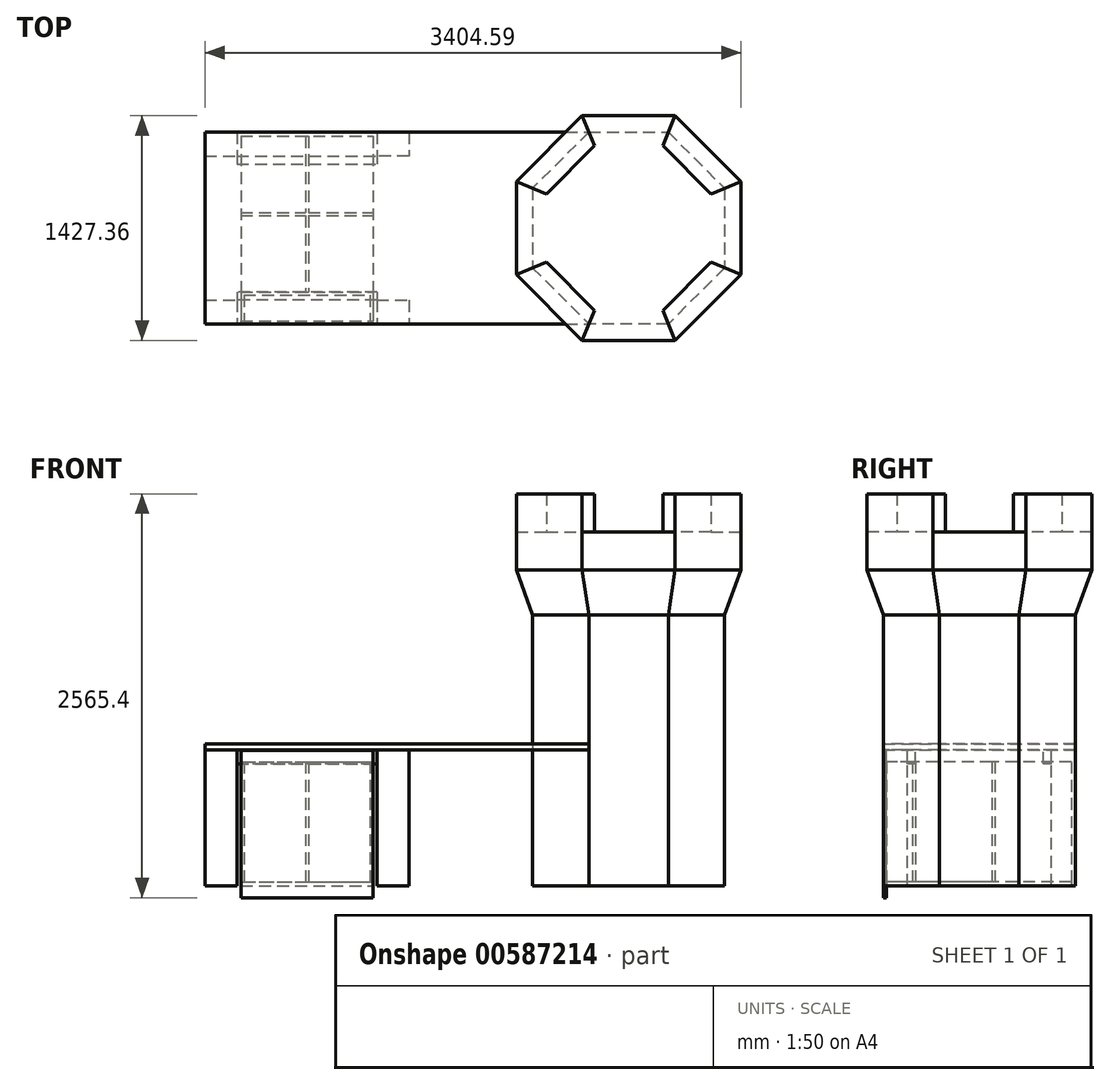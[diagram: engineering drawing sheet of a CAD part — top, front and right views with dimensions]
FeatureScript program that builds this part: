
annotation { "Feature Type Name" : "Feature", "Feature Type Description" : "" }
export const myFeature = defineFeature(function(context is Context, id is Id, definition is map)
    precondition{}
    {
        {
            var Q0;
            Q0=qCreatedBy(makeId("Front.planeOp"),FACE);
            var sketch = newSketch(context, id + "F0", { "sketchPlane" : qUnion([Q0])});
            skLineSegment(sketch, "E0.bottom", {"start": v(1219.2, 0) * mm, "end": v(-1219.2, 0) * mm, "construction": true});
            skLineSegment(sketch, "E0.top", {"start": v(1219.2, -863.6) * mm, "end": v(-1219.2, -863.6) * mm, "construction": true});
            skLineSegment(sketch, "E0.left", {"start": v(1219.2, 0) * mm, "end": v(1219.2, -863.6) * mm, "construction": true});
            skLineSegment(sketch, "E0.right", {"start": v(-1219.2, 0) * mm, "end": v(-1219.2, -863.6) * mm, "construction": true});
            skLineSegment(sketch, "E1", {"start": v(152.4, 0) * mm, "end": v(152.4, -863.6) * mm, "construction": true});
            skLineSegment(sketch, "E2", {"start": v(190.5, 0) * mm, "end": v(190.5, -863.6) * mm, "construction": true});
            skLineSegment(sketch, "E3", {"start": v(-1016, 0) * mm, "end": v(-1016, -863.6) * mm, "construction": true});
            skLineSegment(sketch, "E4", {"start": v(-3657.6, 1778) * mm, "end": v(8534.4, 1778) * mm, "construction": true});
            skLineSegment(sketch, "E5", {"start": v(8534.4, 1778) * mm, "end": v(8534.4, -965.2) * mm, "construction": true});
            skLineSegment(sketch, "E6", {"start": v(8534.4, -965.2) * mm, "end": v(-3657.6, -965.2) * mm, "construction": true});
            skLineSegment(sketch, "E7", {"start": v(-3657.6, -965.2) * mm, "end": v(-3657.6, 1778) * mm, "construction": true});
            skLineSegment(sketch, "E8", {"start": v(-1219.2, 1219.2) * mm, "end": v(1219.2, 1219.2) * mm, "construction": true});
            skLineSegment(sketch, "E9", {"start": v(1054.1, 1143) * mm, "end": v(1054.1, 1625.6) * mm, "construction": true});
            skLineSegment(sketch, "E10", {"start": v(1054.1, 1625.6) * mm, "end": v(2079.7, 1625.6) * mm, "construction": true});
            skLineSegment(sketch, "E11", {"start": v(1054.1, 1143) * mm, "end": v(1219.2, 857.04) * mm, "construction": true});
            skLineSegment(sketch, "E12", {"start": v(1219.2, 857.04) * mm, "end": v(1219.2, 0) * mm, "construction": true});
            skLineSegment(sketch, "E13", {"start": v(1054.1, 1384.3) * mm, "end": v(2079.7, 1384.3) * mm, "construction": true});
            skSolve(sketch);
        }
        {
            var Q0;
            Q0=qCreatedBy(makeId("Top.planeOp"),FACE);
            var sketch = newSketch(context, id + "F1", { "sketchPlane" : qUnion([Q0])});
            skLineSegment(sketch, "E14.bottom", {"start": v(-1219.2, -609.6) * mm, "end": v(1219.2, -609.6) * mm, "construction": true});
            skLineSegment(sketch, "E14.top", {"start": v(-1219.2, 609.6) * mm, "end": v(1219.2, 609.6) * mm, "construction": true});
            skLineSegment(sketch, "E14.left", {"start": v(-1219.2, -609.6) * mm, "end": v(-1219.2, 609.6) * mm, "construction": true});
            skLineSegment(sketch, "E14.right", {"start": v(1219.2, -609.6) * mm, "end": v(1219.2, 609.6) * mm, "construction": true});
            skPoint(sketch, "E14.middle", {"position": v(0, 0) * mm});
            skLineSegment(sketch, "E15", {"start": v(1219.2, 609.6) * mm, "end": v(862.1, 252.5) * mm, "construction": true});
            skLineSegment(sketch, "E16", {"start": v(862.1, 252.5) * mm, "end": v(862.1, -252.5) * mm, "construction": true});
            skLineSegment(sketch, "E17", {"start": v(862.1, -252.5) * mm, "end": v(1219.2, -609.6) * mm, "construction": true});
            skLineSegment(sketch, "E18.bottom", {"start": v(-1219.2, 609.6) * mm, "end": v(-1016, 609.6) * mm, "construction": true});
            skLineSegment(sketch, "E18.top", {"start": v(-1219.2, 457.2) * mm, "end": v(-1016, 457.2) * mm, "construction": true});
            skLineSegment(sketch, "E18.left", {"start": v(-1219.2, 609.6) * mm, "end": v(-1219.2, 457.2) * mm, "construction": true});
            skLineSegment(sketch, "E18.right", {"start": v(-1016, 609.6) * mm, "end": v(-1016, 457.2) * mm, "construction": true});
            skLineSegment(sketch, "E19.bottom", {"start": v(-1219.2, -609.6) * mm, "end": v(-1016, -609.6) * mm, "construction": true});
            skLineSegment(sketch, "E19.top", {"start": v(-1219.2, -457.2) * mm, "end": v(-1016, -457.2) * mm, "construction": true});
            skLineSegment(sketch, "E19.left", {"start": v(-1219.2, -609.6) * mm, "end": v(-1219.2, -457.2) * mm, "construction": true});
            skLineSegment(sketch, "E19.right", {"start": v(-1016, -609.6) * mm, "end": v(-1016, -457.2) * mm, "construction": true});
            skLineSegment(sketch, "E20.bottom", {"start": v(1219.2, 609.6) * mm, "end": v(1016, 609.6) * mm, "construction": true});
            skLineSegment(sketch, "E20.top", {"start": v(1219.2, 457.2) * mm, "end": v(1016, 457.2) * mm, "construction": true});
            skLineSegment(sketch, "E20.left", {"start": v(1219.2, 609.6) * mm, "end": v(1219.2, 457.2) * mm, "construction": true});
            skLineSegment(sketch, "E20.right", {"start": v(1016, 609.6) * mm, "end": v(1016, 457.2) * mm});
            skLineSegment(sketch, "E21.bottom", {"start": v(1219.2, -609.6) * mm, "end": v(1016, -609.6) * mm, "construction": true});
            skLineSegment(sketch, "E21.top", {"start": v(1219.2, -457.2) * mm, "end": v(1016, -457.2) * mm, "construction": true});
            skLineSegment(sketch, "E21.left", {"start": v(1219.2, -609.6) * mm, "end": v(1219.2, -457.2) * mm, "construction": true});
            skLineSegment(sketch, "E21.right", {"start": v(1016, -609.6) * mm, "end": v(1016, -457.2) * mm});
            skLineSegment(sketch, "E22", {"start": v(-1016, 609.6) * mm, "end": v(-1016, -609.6) * mm, "construction": true});
            skLineSegment(sketch, "E23.bottom", {"start": v(-977.9, 406.4) * mm, "end": v(-571.5, 406.4) * mm, "construction": true});
            skLineSegment(sketch, "E23.top", {"start": v(-977.9, 0) * mm, "end": v(-571.5, 0) * mm, "construction": true});
            skLineSegment(sketch, "E23.left", {"start": v(-977.9, 406.4) * mm, "end": v(-977.9, 0) * mm, "construction": true});
            skLineSegment(sketch, "E23.right", {"start": v(-571.5, 406.4) * mm, "end": v(-571.5, 0) * mm, "construction": true});
            skLineSegment(sketch, "E24.top", {"start": v(-571.5, -406.4) * mm, "end": v(-977.9, -406.4) * mm, "construction": true});
            skLineSegment(sketch, "E24.left", {"start": v(-571.5, 0) * mm, "end": v(-571.5, -406.4) * mm, "construction": true});
            skLineSegment(sketch, "E25.top", {"start": v(-571.5, 406.4) * mm, "end": v(-165.1, 406.4) * mm, "construction": true});
            skLineSegment(sketch, "E25.right", {"start": v(-165.1, 0) * mm, "end": v(-165.1, 406.4) * mm, "construction": true});
            skLineSegment(sketch, "E26.bottom", {"start": v(-165.1, 0) * mm, "end": v(-571.5, 0) * mm, "construction": true});
            skLineSegment(sketch, "E26.top", {"start": v(-165.1, -406.4) * mm, "end": v(-571.5, -406.4) * mm, "construction": true});
            skLineSegment(sketch, "E26.left", {"start": v(-165.1, 0) * mm, "end": v(-165.1, -406.4) * mm, "construction": true});
            skLineSegment(sketch, "E27", {"start": v(-571.5, 406.4) * mm, "end": v(-571.5, 609.6) * mm, "construction": true});
            skLineSegment(sketch, "E28", {"start": v(-571.5, -406.4) * mm, "end": v(-571.5, -609.6) * mm, "construction": true});
            skLineSegment(sketch, "E29", {"start": v(-977.9, 0) * mm, "end": v(-977.9, -406.4) * mm, "construction": true});
            skLineSegment(sketch, "E30", {"start": v(1219.2, 609.6) * mm, "end": v(1724.2, 609.6) * mm, "construction": true});
            skLineSegment(sketch, "E31", {"start": v(1724.2, 609.6) * mm, "end": v(2081.3, 252.5) * mm, "construction": true});
            skLineSegment(sketch, "E32", {"start": v(2081.3, 252.5) * mm, "end": v(2081.3, -252.5) * mm, "construction": true});
            skLineSegment(sketch, "E33", {"start": v(2081.3, -252.5) * mm, "end": v(1724.2, -609.6) * mm, "construction": true});
            skLineSegment(sketch, "E34", {"start": v(1724.2, -609.6) * mm, "end": v(1219.2, -609.6) * mm, "construction": true});
            skLineSegment(sketch, "E35", {"start": v(-127, 609.6) * mm, "end": v(-127, -609.6) * mm, "construction": true});
            skLineSegment(sketch, "E36.bottom", {"start": v(-127, 609.6) * mm, "end": v(76.2, 609.6) * mm, "construction": true});
            skLineSegment(sketch, "E36.top", {"start": v(-127, 457.2) * mm, "end": v(76.2, 457.2) * mm, "construction": true});
            skLineSegment(sketch, "E36.left", {"start": v(-127, 609.6) * mm, "end": v(-127, 457.2) * mm, "construction": true});
            skLineSegment(sketch, "E36.right", {"start": v(76.2, 609.6) * mm, "end": v(76.2, 457.2) * mm, "construction": true});
            skLineSegment(sketch, "E37.bottom", {"start": v(-127, -609.6) * mm, "end": v(76.2, -609.6) * mm, "construction": true});
            skLineSegment(sketch, "E37.top", {"start": v(-127, -457.2) * mm, "end": v(76.2, -457.2) * mm, "construction": true});
            skLineSegment(sketch, "E37.left", {"start": v(-127, -609.6) * mm, "end": v(-127, -457.2) * mm, "construction": true});
            skLineSegment(sketch, "E37.right", {"start": v(76.2, -609.6) * mm, "end": v(76.2, -457.2) * mm, "construction": true});
            skSolve(sketch);
        }
        {
            var Q0;
            Q0=qCreatedBy(makeId("Top.planeOp"),FACE);
            var sketch = newSketch(context, id + "F2", { "sketchPlane" : qUnion([Q0])});
            skLineSegment(sketch, "E38.bottom", {"start": v(-1219.2, -609.6) * mm, "end": v(1219.2, -609.6) * mm});
            skLineSegment(sketch, "E38.top", {"start": v(-1219.2, 609.6) * mm, "end": v(1219.2, 609.6) * mm});
            skLineSegment(sketch, "E38.left", {"start": v(-1219.2, -609.6) * mm, "end": v(-1219.2, 609.6) * mm});
            skLineSegment(sketch, "E38.right", {"start": v(1219.2, -609.6) * mm, "end": v(1219.2, 609.6) * mm, "construction": true});
            skLineSegment(sketch, "E39.0", {"start": v(1219.2, 609.6) * mm, "end": v(862.1, 252.5) * mm});
            skLineSegment(sketch, "E40.0", {"start": v(862.1, 252.5) * mm, "end": v(862.1, -252.5) * mm});
            skLineSegment(sketch, "E40.1", {"start": v(862.1, -252.5) * mm, "end": v(1219.2, -609.6) * mm});
            skSolve(sketch);
        }
        {
            var Q0;
            Q0 = qSketchRegion(id + "F2", true);
            extrude(context, id + "F3", {"entities" : qUnion([Q0]), "depth" : 38.1 * mm, "offsetDistance" : 25.4 * mm});
        }
        {
            var Q0;
            Q0=qCreatedBy(makeId("Top.planeOp"),FACE);
            var sketch = newSketch(context, id + "F4", { "sketchPlane" : qUnion([Q0])});
            skLineSegment(sketch, "E41.bottom", {"start": v(-1219.2, 609.6) * mm, "end": v(-1016, 609.6) * mm});
            skLineSegment(sketch, "E41.top", {"start": v(-1219.2, 457.2) * mm, "end": v(-1016, 457.2) * mm});
            skLineSegment(sketch, "E41.left", {"start": v(-1219.2, 609.6) * mm, "end": v(-1219.2, 457.2) * mm});
            skLineSegment(sketch, "E41.right", {"start": v(-1016, 609.6) * mm, "end": v(-1016, 457.2) * mm});
            skLineSegment(sketch, "E42.bottom", {"start": v(-1219.2, -457.2) * mm, "end": v(-1016, -457.2) * mm});
            skLineSegment(sketch, "E42.top", {"start": v(-1219.2, -609.6) * mm, "end": v(-1016, -609.6) * mm});
            skLineSegment(sketch, "E42.left", {"start": v(-1219.2, -457.2) * mm, "end": v(-1219.2, -609.6) * mm});
            skLineSegment(sketch, "E42.right", {"start": v(-1016, -457.2) * mm, "end": v(-1016, -609.6) * mm});
            skLineSegment(sketch, "E43.bottom", {"start": v(76.2, 609.6) * mm, "end": v(-127, 609.6) * mm});
            skLineSegment(sketch, "E43.top", {"start": v(76.2, 457.2) * mm, "end": v(-127, 457.2) * mm});
            skLineSegment(sketch, "E43.left", {"start": v(76.2, 609.6) * mm, "end": v(76.2, 457.2) * mm});
            skLineSegment(sketch, "E43.right", {"start": v(-127, 609.6) * mm, "end": v(-127, 457.2) * mm});
            skLineSegment(sketch, "E44.bottom", {"start": v(-127, -457.2) * mm, "end": v(76.2, -457.2) * mm});
            skLineSegment(sketch, "E44.top", {"start": v(-127, -609.6) * mm, "end": v(76.2, -609.6) * mm});
            skLineSegment(sketch, "E44.left", {"start": v(-127, -457.2) * mm, "end": v(-127, -609.6) * mm});
            skLineSegment(sketch, "E44.right", {"start": v(76.2, -457.2) * mm, "end": v(76.2, -609.6) * mm});
            skSolve(sketch);
        }
        {
            var Q0;
            Q0 = qSketchRegion(id + "F4", true);
            var Q1;
            Q1=sQuery(id+"F0.wireOp",VERTEX,"E0.right.end");
            extrude(context, id + "F5", {"entities" : qUnion([Q0]), "endBound" : BoundingType.UP_TO_VERTEX, "oppositeDirection" : true, "depth" : 25.4 * mm, "endBoundEntityVertex" : qUnion([Q1]), "offsetDistance" : 25.4 * mm});
        }
        {
            var Q0;
            Q0=qCreatedBy(makeId("Front.planeOp"),FACE);
            var Q1;
            Q1=sQuery(id+"F1.wireOp",VERTEX,"E14.left.start");
            cPlane(context, id + "F6", {"entities" : qUnion([Q0, Q1]), "cplaneType" : CPlaneType.PLANE_POINT, "offset" : 25.4 * mm, "width" : 152.4 * mm, "height" : 152.4 * mm});
        }
        {
            var Q0;
            Q0=qCreatedBy(makeId("Top.planeOp"),FACE);
            var sketch = newSketch(context, id + "F7", { "sketchPlane" : qUnion([Q0])});
            skLineSegment(sketch, "E45.0", {"start": v(1724.2, -609.6) * mm, "end": v(1219.2, -609.6) * mm});
            skLineSegment(sketch, "E45.1", {"start": v(2081.3, -252.5) * mm, "end": v(1724.2, -609.6) * mm});
            skLineSegment(sketch, "E45.2", {"start": v(2081.3, 252.5) * mm, "end": v(2081.3, -252.5) * mm});
            skLineSegment(sketch, "E45.3", {"start": v(1724.2, 609.6) * mm, "end": v(2081.3, 252.5) * mm});
            skLineSegment(sketch, "E45.4", {"start": v(1219.2, 609.6) * mm, "end": v(1724.2, 609.6) * mm});
            skLineSegment(sketch, "E45.5", {"start": v(1219.2, 609.6) * mm, "end": v(862.1, 252.5) * mm});
            skLineSegment(sketch, "E45.6", {"start": v(862.1, 252.5) * mm, "end": v(862.1, -252.5) * mm});
            skLineSegment(sketch, "E45.7", {"start": v(862.1, -252.5) * mm, "end": v(1219.2, -609.6) * mm});
            skSolve(sketch);
        }
        {
            var Q0;
            Q0=makeQuery(id+"F7.imprint","IMPRINT",FACE,{"disambiguationData":[TD([[makeQuery(id+"F7.imprint","IMPRINT",EDGE,{"derivedFrom":sQuery(id+"F7.wireOp",EDGE,"E45.0")}),-1.0]])]});
            var Q1;
            Q1 = qConstructionFilter(qBodyType(qCreatedBy(id + "F7" ,EDGE), BodyType.WIRE), ConstructionObject.NO);
            var Q2;
            Q2=sQuery(id+"F0.wireOp",VERTEX,"E0.left.end");
            var Q3;
            Q3=sQuery(id+"F0.wireOp",VERTEX,"E12.start");
            extrude(context, id + "F8", {"entities" : qUnion([Q0]), "surfaceEntities" : qUnion([Q1]), "endBound" : BoundingType.UP_TO_VERTEX, "oppositeDirection" : true, "depth" : 25.4 * mm, "endBoundEntityVertex" : qUnion([Q2]), "offsetDistance" : 25.4 * mm, "hasSecondDirection" : true, "secondDirectionBound" : SecondDirectionBoundingType.UP_TO_VERTEX, "secondDirectionOppositeDirection" : false, "secondDirectionDepth" : 25.4 * mm, "secondDirectionBoundEntityVertex" : qUnion([Q3])});
        }
        {
            var Q0;
            Q0=makeQuery(id+"F8.opExtrude","CAP_FACE",FACE,{"disambiguationData":[OSD([sQuery(id+"F7.wireOp",EDGE,"E45.0"),sQuery(id+"F7.wireOp",EDGE,"E45.1"),sQuery(id+"F7.wireOp",EDGE,"E45.2"),sQuery(id+"F7.wireOp",EDGE,"E45.3"),sQuery(id+"F7.wireOp",EDGE,"E45.4"),sQuery(id+"F7.wireOp",EDGE,"E45.5"),sQuery(id+"F7.wireOp",EDGE,"E45.6"),sQuery(id+"F7.wireOp",EDGE,"E45.7")])],"isStart":true});
            var sketch = newSketch(context, id + "F9", { "sketchPlane" : qUnion([Q0])});
            skSolve(sketch);
        }
        {
            var Q0;
            Q0 = qSketchRegion(id + "F9", true);
            var Q1;
            Q1=makeQuery(id+"F9.imprint","IMPRINT",FACE,{"disambiguationData":[TD([[makeQuery(id+"F9.imprint","IMPRINT",EDGE,{"derivedFrom":makeQuery(id+"F8.opExtrude","CAP_EDGE",EDGE,{"disambiguationData":[OSD([sQuery(id+"F7.wireOp",EDGE,"E45.0")])],"isStart":true})}),-1.0]])]});
            var Q2;
            Q2=sQuery(id+"F0.wireOp",VERTEX,"E9.start");
            extrude(context, id + "F10", {"entities" : qUnion([Q0, Q1]), "operationType" : NewBodyOperationType.ADD, "endBound" : BoundingType.UP_TO_VERTEX, "depth" : 25.4 * mm, "endBoundEntityVertex" : qUnion([Q2]), "offsetDistance" : 25.4 * mm, "hasDraft" : true, "draftAngle" : 20 * degree});
        }
        {
            var Q0;
            Q0=makeQuery(id+"F10.opExtrude","CAP_FACE",FACE,{"disambiguationData":[OSD([sQuery(id+"F7.wireOp",EDGE,"E45.0"),sQuery(id+"F7.wireOp",EDGE,"E45.1"),sQuery(id+"F7.wireOp",EDGE,"E45.2"),sQuery(id+"F7.wireOp",EDGE,"E45.3"),sQuery(id+"F7.wireOp",EDGE,"E45.4"),sQuery(id+"F7.wireOp",EDGE,"E45.5"),sQuery(id+"F7.wireOp",EDGE,"E45.6"),sQuery(id+"F7.wireOp",EDGE,"E45.7")])],"isStart":false});
            var sketch = newSketch(context, id + "F11", { "sketchPlane" : qUnion([Q0])});
            skLineSegment(sketch, "E46.0", {"start": v(1176.09, 713.68) * mm, "end": v(758.02, 295.62) * mm});
            skLineSegment(sketch, "E46.1", {"start": v(1176.09, 713.68) * mm, "end": v(1767.32, 713.68) * mm});
            skLineSegment(sketch, "E46.2", {"start": v(1767.32, 713.68) * mm, "end": v(2185.39, 295.62) * mm});
            skLineSegment(sketch, "E46.3", {"start": v(2185.39, 295.62) * mm, "end": v(2185.39, -295.62) * mm});
            skLineSegment(sketch, "E46.4", {"start": v(2185.39, -295.62) * mm, "end": v(1767.32, -713.68) * mm});
            skLineSegment(sketch, "E46.5", {"start": v(1767.32, -713.68) * mm, "end": v(1176.09, -713.68) * mm});
            skLineSegment(sketch, "E46.6", {"start": v(758.02, -295.62) * mm, "end": v(1176.09, -713.68) * mm});
            skLineSegment(sketch, "E46.7", {"start": v(758.02, 295.62) * mm, "end": v(758.02, -295.62) * mm});
            skSolve(sketch);
        }
        {
            var Q0;
            Q0 = qSketchRegion(id + "F11", true);
            var Q1;
            Q1=sQuery(id+"F0.wireOp",VERTEX,"E13.start");
            extrude(context, id + "F12", {"entities" : qUnion([Q0]), "operationType" : NewBodyOperationType.ADD, "endBound" : BoundingType.UP_TO_VERTEX, "depth" : 25.4 * mm, "endBoundEntityVertex" : qUnion([Q1]), "offsetDistance" : 25.4 * mm});
        }
        {
            var Q0;
            Q0=makeQuery(id+"F12.opExtrude","CAP_FACE",FACE,{"disambiguationData":[OSD([sQuery(id+"F11.wireOp",EDGE,"E46.0"),sQuery(id+"F11.wireOp",EDGE,"E46.1"),sQuery(id+"F11.wireOp",EDGE,"E46.2"),sQuery(id+"F11.wireOp",EDGE,"E46.3"),sQuery(id+"F11.wireOp",EDGE,"E46.4"),sQuery(id+"F11.wireOp",EDGE,"E46.5"),sQuery(id+"F11.wireOp",EDGE,"E46.6"),sQuery(id+"F11.wireOp",EDGE,"E46.7")])],"isStart":false});
            var sketch = newSketch(context, id + "F13", { "sketchPlane" : qUnion([Q0])});
            skLineSegment(sketch, "E47.0", {"start": v(1176.09, 713.68) * mm, "end": v(758.02, 295.62) * mm});
            skLineSegment(sketch, "E47.1", {"start": v(1176.09, 713.68) * mm, "end": v(1767.32, 713.68) * mm, "construction": true});
            skLineSegment(sketch, "E47.2", {"start": v(1767.32, 713.68) * mm, "end": v(2185.39, 295.62) * mm});
            skLineSegment(sketch, "E47.3", {"start": v(2185.39, 295.62) * mm, "end": v(2185.39, -295.62) * mm, "construction": true});
            skLineSegment(sketch, "E47.4", {"start": v(2185.39, -295.62) * mm, "end": v(1767.32, -713.68) * mm});
            skLineSegment(sketch, "E47.5", {"start": v(1767.32, -713.68) * mm, "end": v(1176.09, -713.68) * mm, "construction": true});
            skLineSegment(sketch, "E47.6", {"start": v(758.02, -295.62) * mm, "end": v(1176.09, -713.68) * mm});
            skLineSegment(sketch, "E47.7", {"start": v(758.02, 295.62) * mm, "end": v(758.02, -295.62) * mm, "construction": true});
            skLineSegment(sketch, "E48.0", {"start": v(1255, 523.18) * mm, "end": v(948.52, 216.7) * mm});
            skLineSegment(sketch, "E48.1", {"start": v(948.52, 216.7) * mm, "end": v(948.52, -216.7) * mm, "construction": true});
            skLineSegment(sketch, "E48.2", {"start": v(1255, 523.18) * mm, "end": v(1688.41, 523.18) * mm, "construction": true});
            skLineSegment(sketch, "E48.3", {"start": v(948.52, -216.7) * mm, "end": v(1255, -523.18) * mm});
            skLineSegment(sketch, "E48.4", {"start": v(1688.41, 523.18) * mm, "end": v(1994.89, 216.7) * mm});
            skLineSegment(sketch, "E48.5", {"start": v(1994.89, 216.7) * mm, "end": v(1994.89, -216.7) * mm, "construction": true});
            skLineSegment(sketch, "E48.6", {"start": v(1994.89, -216.7) * mm, "end": v(1688.41, -523.18) * mm});
            skLineSegment(sketch, "E48.7", {"start": v(1688.41, -523.18) * mm, "end": v(1255, -523.18) * mm, "construction": true});
            skLineSegment(sketch, "E49", {"start": v(1176.09, 713.68) * mm, "end": v(1255, 523.18) * mm});
            skLineSegment(sketch, "E50", {"start": v(1767.32, 713.68) * mm, "end": v(1688.41, 523.18) * mm});
            skLineSegment(sketch, "E51", {"start": v(1994.89, 216.7) * mm, "end": v(2185.39, 295.62) * mm});
            skLineSegment(sketch, "E52", {"start": v(1994.89, -216.7) * mm, "end": v(2185.39, -295.62) * mm});
            skLineSegment(sketch, "E53", {"start": v(1688.41, -523.18) * mm, "end": v(1767.32, -713.68) * mm});
            skLineSegment(sketch, "E54", {"start": v(1255, -523.18) * mm, "end": v(1176.09, -713.68) * mm});
            skLineSegment(sketch, "E55", {"start": v(948.52, -216.7) * mm, "end": v(758.02, -295.62) * mm});
            skLineSegment(sketch, "E56", {"start": v(758.02, 295.62) * mm, "end": v(948.52, 216.7) * mm});
            skSolve(sketch);
        }
        {
            var Q0;
            Q0 = qSketchRegion(id + "F13", true);
            var Q1;
            Q1=sQuery(id+"F0.wireOp",VERTEX,"E9.end");
            extrude(context, id + "F14", {"entities" : qUnion([Q0]), "operationType" : NewBodyOperationType.ADD, "endBound" : BoundingType.UP_TO_VERTEX, "depth" : 25.4 * mm, "endBoundEntityVertex" : qUnion([Q1]), "offsetDistance" : 25.4 * mm});
        }
        {
            var Q0;
            Q0=qCreatedBy(makeId("Top.planeOp"),FACE);
            var sketch = newSketch(context, id + "F15", { "sketchPlane" : qUnion([Q0])});
            skLineSegment(sketch, "E57.bottom", {"start": v(-1016, 457.2) * mm, "end": v(-127, 457.2) * mm});
            skLineSegment(sketch, "E57.top", {"start": v(-1016, 406.4) * mm, "end": v(-127, 406.4) * mm});
            skLineSegment(sketch, "E57.left", {"start": v(-1016, 457.2) * mm, "end": v(-1016, 406.4) * mm});
            skLineSegment(sketch, "E57.right", {"start": v(-127, 457.2) * mm, "end": v(-127, 406.4) * mm});
            skLineSegment(sketch, "E58.bottom", {"start": v(-127, 406.4) * mm, "end": v(-165.1, 406.4) * mm});
            skLineSegment(sketch, "E58.top", {"start": v(-127, -406.4) * mm, "end": v(-165.1, -406.4) * mm});
            skLineSegment(sketch, "E58.left", {"start": v(-127, 406.4) * mm, "end": v(-127, -406.4) * mm});
            skLineSegment(sketch, "E58.right", {"start": v(-165.1, 406.4) * mm, "end": v(-165.1, -406.4) * mm});
            skLineSegment(sketch, "E59.bottom", {"start": v(-127, -406.4) * mm, "end": v(-1016, -406.4) * mm});
            skLineSegment(sketch, "E59.top", {"start": v(-127, -457.2) * mm, "end": v(-1016, -457.2) * mm});
            skLineSegment(sketch, "E59.left", {"start": v(-127, -406.4) * mm, "end": v(-127, -457.2) * mm});
            skLineSegment(sketch, "E59.right", {"start": v(-1016, -406.4) * mm, "end": v(-1016, -457.2) * mm});
            skLineSegment(sketch, "E60.bottom", {"start": v(-1016, -406.4) * mm, "end": v(-977.9, -406.4) * mm});
            skLineSegment(sketch, "E60.top", {"start": v(-1016, 406.4) * mm, "end": v(-977.9, 406.4) * mm});
            skLineSegment(sketch, "E60.left", {"start": v(-1016, -406.4) * mm, "end": v(-1016, 406.4) * mm});
            skLineSegment(sketch, "E60.right", {"start": v(-977.9, -406.4) * mm, "end": v(-977.9, 406.4) * mm});
            skSolve(sketch);
        }
        {
            var Q0;
            Q0=makeQuery(id+"F15.imprint","IMPRINT",FACE,{"disambiguationData":[TD([[makeQuery(id+"F15.imprint","IMPRINT",EDGE,{"derivedFrom":sQuery(id+"F15.wireOp",EDGE,"E58.bottom")}),1.0]])]});
            var Q1;
            Q1=makeQuery(id+"F15.imprint","IMPRINT",FACE,{"disambiguationData":[TD([[makeQuery(id+"F15.imprint","IMPRINT",EDGE,{"derivedFrom":sQuery(id+"F15.wireOp",EDGE,"E59.top")}),-1.0]])]});
            var Q2;
            Q2=makeQuery(id+"F15.imprint","IMPRINT",FACE,{"disambiguationData":[TD([[makeQuery(id+"F15.imprint","IMPRINT",EDGE,{"derivedFrom":sQuery(id+"F15.wireOp",EDGE,"E60.bottom")}),1.0]])]});
            var Q3;
            Q3=makeQuery(id+"F15.imprint","IMPRINT",FACE,{"disambiguationData":[TD([[makeQuery(id+"F15.imprint","IMPRINT",EDGE,{"derivedFrom":sQuery(id+"F15.wireOp",EDGE,"E57.bottom")}),-1.0]])]});
            extrude(context, id + "F16", {"entities" : qUnion([Q0, Q1, Q2, Q3]), "oppositeDirection" : true, "depth" : 88.9 * mm, "offsetDistance" : 25.4 * mm});
        }
        {
            var Q0;
            Q0=qCreatedBy(makeId("Top.planeOp"),FACE);
            var Q1;
            Q1=sQuery(id+"F0.wireOp",VERTEX,"E0.right.end");
            cPlane(context, id + "F17", {"entities" : qUnion([Q0, Q1]), "cplaneType" : CPlaneType.PLANE_POINT, "offset" : 25.4 * mm, "width" : 152.4 * mm, "height" : 152.4 * mm});
        }
        {
            var Q0;
            Q0=qCreatedBy(id+"F17.planeOp",FACE);
            var sketch = newSketch(context, id + "F18", { "sketchPlane" : qUnion([Q0])});
            skLineSegment(sketch, "E61.bottom", {"start": v(-990.6, 584.2) * mm, "end": v(-152.4, 584.2) * mm});
            skLineSegment(sketch, "E61.top", {"start": v(-990.6, -590.55) * mm, "end": v(-152.4, -590.55) * mm});
            skLineSegment(sketch, "E61.left", {"start": v(-990.6, 584.2) * mm, "end": v(-990.6, -590.55) * mm});
            skLineSegment(sketch, "E61.right", {"start": v(-152.4, 584.2) * mm, "end": v(-152.4, -590.55) * mm});
            skLineSegment(sketch, "E62.bottom", {"start": v(-1016, -457.2) * mm, "end": v(-127, -457.2) * mm, "construction": true});
            skLineSegment(sketch, "E62.top", {"start": v(-1016, 457.2) * mm, "end": v(-127, 457.2) * mm, "construction": true});
            skLineSegment(sketch, "E62.left", {"start": v(-1016, -457.2) * mm, "end": v(-1016, 457.2) * mm, "construction": true});
            skLineSegment(sketch, "E62.right", {"start": v(-127, -457.2) * mm, "end": v(-127, 457.2) * mm, "construction": true});
            skSolve(sketch);
        }
        {
            var Q0;
            Q0 = qSketchRegion(id + "F18", true);
            extrude(context, id + "F19", {"entities" : qUnion([Q0]), "depth" : 25.4 * mm, "offsetDistance" : 25.4 * mm});
        }
        {
            var Q0;
            Q0=qCreatedBy(makeId("Front.planeOp"),FACE);
            var Q1;
            Q1=makeQuery(id+"F19.opExtrude","CAP_VERTEX",VERTEX,{"disambiguationData":[OSD([sQuery(id+"F18.wireOp",EDGE,"E61.top"),sQuery(id+"F18.wireOp",EDGE,"E61.left")])],"isStart":true});
            cPlane(context, id + "F20", {"entities" : qUnion([Q0, Q1]), "cplaneType" : CPlaneType.PLANE_POINT, "offset" : 25.4 * mm, "width" : 152.4 * mm, "height" : 152.4 * mm});
        }
        {
            var Q0;
            Q0=qCreatedBy(id+"F20.planeOp",FACE);
            var sketch = newSketch(context, id + "F21", { "sketchPlane" : qUnion([Q0])});
            skLineSegment(sketch, "E63.bottom", {"start": v(-990.6, -939.8) * mm, "end": v(-152.4, -939.8) * mm});
            skLineSegment(sketch, "E63.top", {"start": v(-990.6, -3.18) * mm, "end": v(-152.4, -3.18) * mm});
            skLineSegment(sketch, "E63.left", {"start": v(-990.6, -939.8) * mm, "end": v(-990.6, -3.17) * mm});
            skLineSegment(sketch, "E63.right", {"start": v(-152.4, -939.8) * mm, "end": v(-152.4, -3.17) * mm});
            skSolve(sketch);
        }
        {
            var Q0;
            Q0 = qSketchRegion(id + "F21", true);
            var Q1;
            Q1=sQuery(id+"F1.wireOp",VERTEX,"E14.left.start");
            extrude(context, id + "F22", {"entities" : qUnion([Q0]), "endBound" : BoundingType.UP_TO_VERTEX, "depth" : 25.4 * mm, "endBoundEntityVertex" : qUnion([Q1]), "offsetDistance" : 25.4 * mm});
        }
        {
            var Q0;
            Q0=makeQuery(id+"F19.opExtrude","CAP_FACE",FACE,{"disambiguationData":[OSD([sQuery(id+"F18.wireOp",EDGE,"E61.bottom"),sQuery(id+"F18.wireOp",EDGE,"E61.top"),sQuery(id+"F18.wireOp",EDGE,"E61.left"),sQuery(id+"F18.wireOp",EDGE,"E61.right")])],"isStart":false});
            var sketch = newSketch(context, id + "F23", { "sketchPlane" : qUnion([Q0])});
            skLineSegment(sketch, "E64.bottom", {"start": v(-990.6, -406.4) * mm, "end": v(-152.4, -406.4) * mm});
            skLineSegment(sketch, "E64.top", {"start": v(-990.6, -425.45) * mm, "end": v(-152.4, -425.45) * mm});
            skLineSegment(sketch, "E64.left", {"start": v(-990.6, -406.4) * mm, "end": v(-990.6, -425.45) * mm});
            skLineSegment(sketch, "E64.right", {"start": v(-152.4, -406.4) * mm, "end": v(-152.4, -425.45) * mm});
            skLineSegment(sketch, "E65.bottom", {"start": v(-990.6, -425.45) * mm, "end": v(-971.55, -425.45) * mm});
            skLineSegment(sketch, "E65.top", {"start": v(-990.6, -590.55) * mm, "end": v(-971.55, -590.55) * mm});
            skLineSegment(sketch, "E65.left", {"start": v(-990.6, -425.45) * mm, "end": v(-990.6, -590.55) * mm});
            skLineSegment(sketch, "E65.right", {"start": v(-971.55, -425.45) * mm, "end": v(-971.55, -590.55) * mm});
            skLineSegment(sketch, "E66.bottom", {"start": v(-152.4, -425.45) * mm, "end": v(-171.45, -425.45) * mm});
            skLineSegment(sketch, "E66.top", {"start": v(-152.4, -590.55) * mm, "end": v(-171.45, -590.55) * mm});
            skLineSegment(sketch, "E66.left", {"start": v(-152.4, -425.45) * mm, "end": v(-152.4, -590.55) * mm});
            skLineSegment(sketch, "E66.right", {"start": v(-171.45, -425.45) * mm, "end": v(-171.45, -590.55) * mm});
            skSolve(sketch);
        }
        {
            var Q0;
            Q0 = qSketchRegion(id + "F23", true);
            extrude(context, id + "F24", {"entities" : qUnion([Q0]), "depth" : 762 * mm, "offsetDistance" : 25.4 * mm});
        }
        {
            var Q0;
            Q0=makeQuery(id+"F19.opExtrude","CAP_FACE",FACE,{"disambiguationData":[OSD([sQuery(id+"F18.wireOp",EDGE,"E61.bottom"),sQuery(id+"F18.wireOp",EDGE,"E61.top"),sQuery(id+"F18.wireOp",EDGE,"E61.left"),sQuery(id+"F18.wireOp",EDGE,"E61.right")])],"isStart":false});
            var sketch = newSketch(context, id + "F25", { "sketchPlane" : qUnion([Q0])});
            skLineSegment(sketch, "E67.bottom", {"start": v(-581.02, 584.2) * mm, "end": v(-561.97, 584.2) * mm});
            skLineSegment(sketch, "E67.top", {"start": v(-581.02, -406.4) * mm, "end": v(-561.97, -406.4) * mm});
            skLineSegment(sketch, "E67.left", {"start": v(-581.02, 584.2) * mm, "end": v(-581.02, -406.4) * mm});
            skLineSegment(sketch, "E67.right", {"start": v(-561.97, 584.2) * mm, "end": v(-561.97, -406.4) * mm});
            skLineSegment(sketch, "E68.bottom", {"start": v(-990.6, 79.38) * mm, "end": v(-152.4, 79.38) * mm});
            skLineSegment(sketch, "E68.top", {"start": v(-990.6, 98.43) * mm, "end": v(-152.4, 98.43) * mm});
            skLineSegment(sketch, "E68.left", {"start": v(-990.6, 79.38) * mm, "end": v(-990.6, 98.43) * mm});
            skLineSegment(sketch, "E68.right", {"start": v(-152.4, 79.38) * mm, "end": v(-152.4, 98.43) * mm});
            skLineSegment(sketch, "E69", {"start": v(-581.02, 88.9) * mm, "end": v(-561.97, 88.9) * mm, "construction": true});
            skSolve(sketch);
        }
        {
            var Q0;
            Q0 = qSketchRegion(id + "F25", true);
            extrude(context, id + "F26", {"entities" : qUnion([Q0]), "depth" : 762 * mm, "offsetDistance" : 25.4 * mm});
        }
    });
